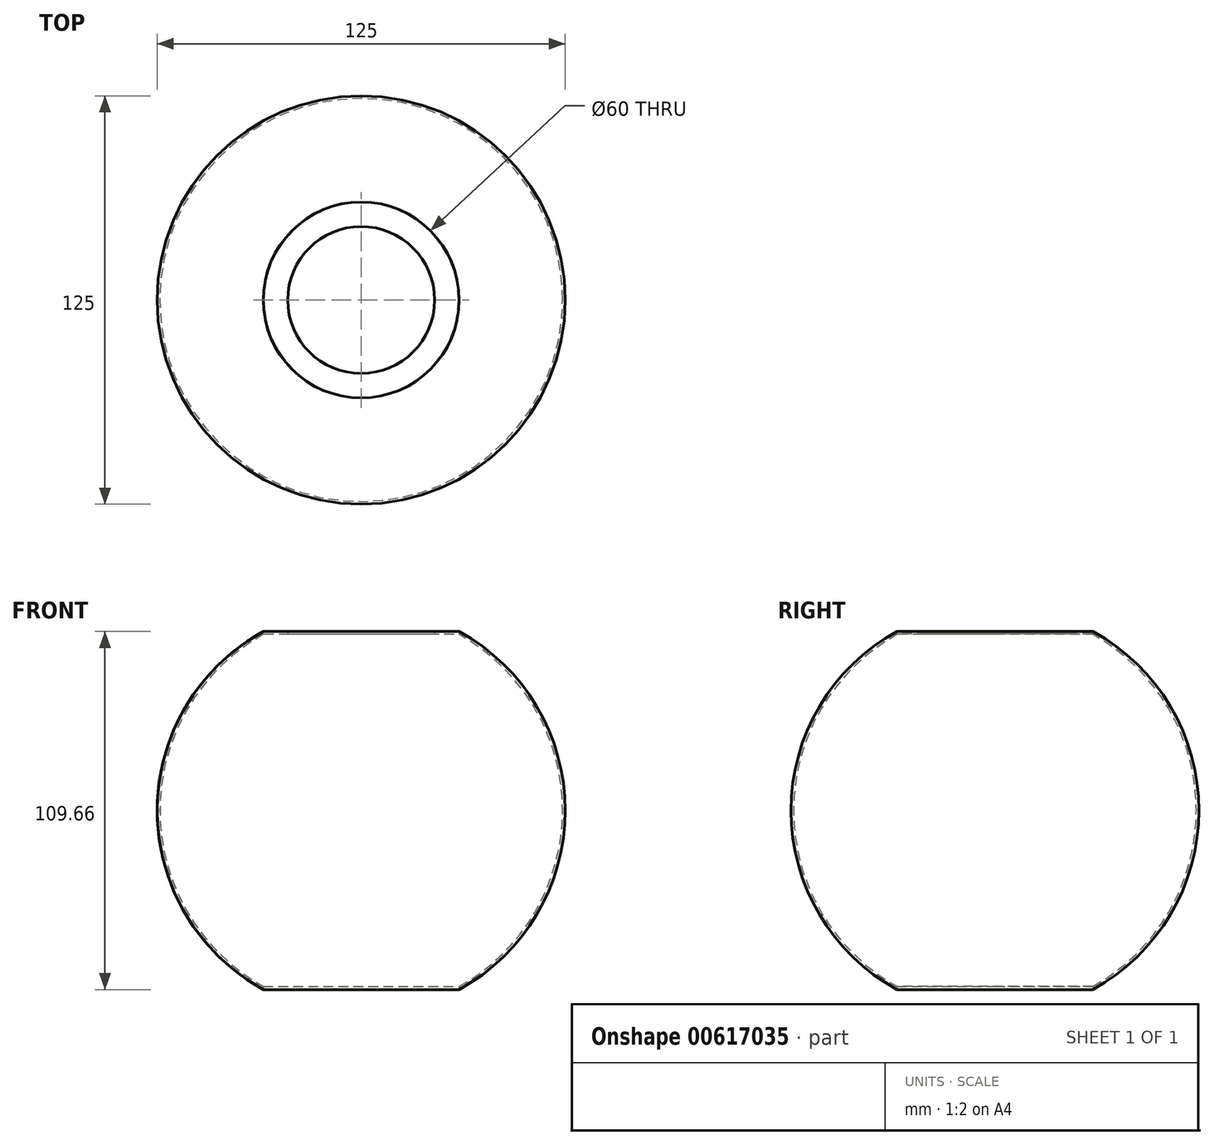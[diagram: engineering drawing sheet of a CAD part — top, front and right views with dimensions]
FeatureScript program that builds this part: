
annotation { "Feature Type Name" : "Feature", "Feature Type Description" : "" }
export const myFeature = defineFeature(function(context is Context, id is Id, definition is map)
    precondition{}
    {
        {
            var Q0;
            Q0=qCreatedBy(makeId("Front.planeOp"),FACE);
            var sketch = newSketch(context, id + "F0", { "sketchPlane" : qUnion([Q0])});
            skCircle(sketch, "E0", {"center": v(0, 0) * mm, "radius": 62.5 * mm, "construction": true});
            skLineSegment(sketch, "E1", {"start": v(0, 54.83) * mm, "end": v(30, 54.83) * mm, "construction": true});
            skLineSegment(sketch, "E2", {"start": v(22.5, 54.83) * mm, "end": v(30, 54.83) * mm});
            skLineSegment(sketch, "E3.3", {"start": v(22.5, 54.03) * mm, "end": v(29.8, 54.03) * mm});
            skLineSegment(sketch, "E4", {"start": v(22.5, 54.03) * mm, "end": v(22.5, 54.83) * mm});
            skLineSegment(sketch, "E5", {"start": v(0, -54.83) * mm, "end": v(0, 54.83) * mm, "construction": true});
            skLineSegment(sketch, "E6", {"start": v(30, -54.83) * mm, "end": v(0, -54.83) * mm, "construction": true});
            skArc(sketch, "E7", {"start": v(30, -54.83) * mm, "mid": v(62.5, 0) * mm, "end": v(30, 54.83) * mm});
            skArc(sketch, "E8.0", {"start": v(30, -53.92) * mm, "mid": v(61.7, 0.12) * mm, "end": v(29.8, 54.03) * mm});
            skLineSegment(sketch, "E9", {"start": v(30, -54.83) * mm, "end": v(30, -53.92) * mm});
            skSolve(sketch);
        }
        {
            var Q0;
            Q0=makeQuery(id+"F0.imprint","IMPRINT",FACE,{"disambiguationData":[TD([[makeQuery(id+"F0.imprint","IMPRINT",EDGE,{"derivedFrom":sQuery(id+"F0.wireOp",EDGE,"E2")}),-1.0]])]});
            var Q1;
            Q1=sQuery(id+"F0.wireOp",EDGE,"E5");
            revolve(context, id + "F1", {"entities" : qUnion([Q0]), "axis" : qUnion([Q1]), "revolveType" : RevolveType.FULL});
        }
    });
